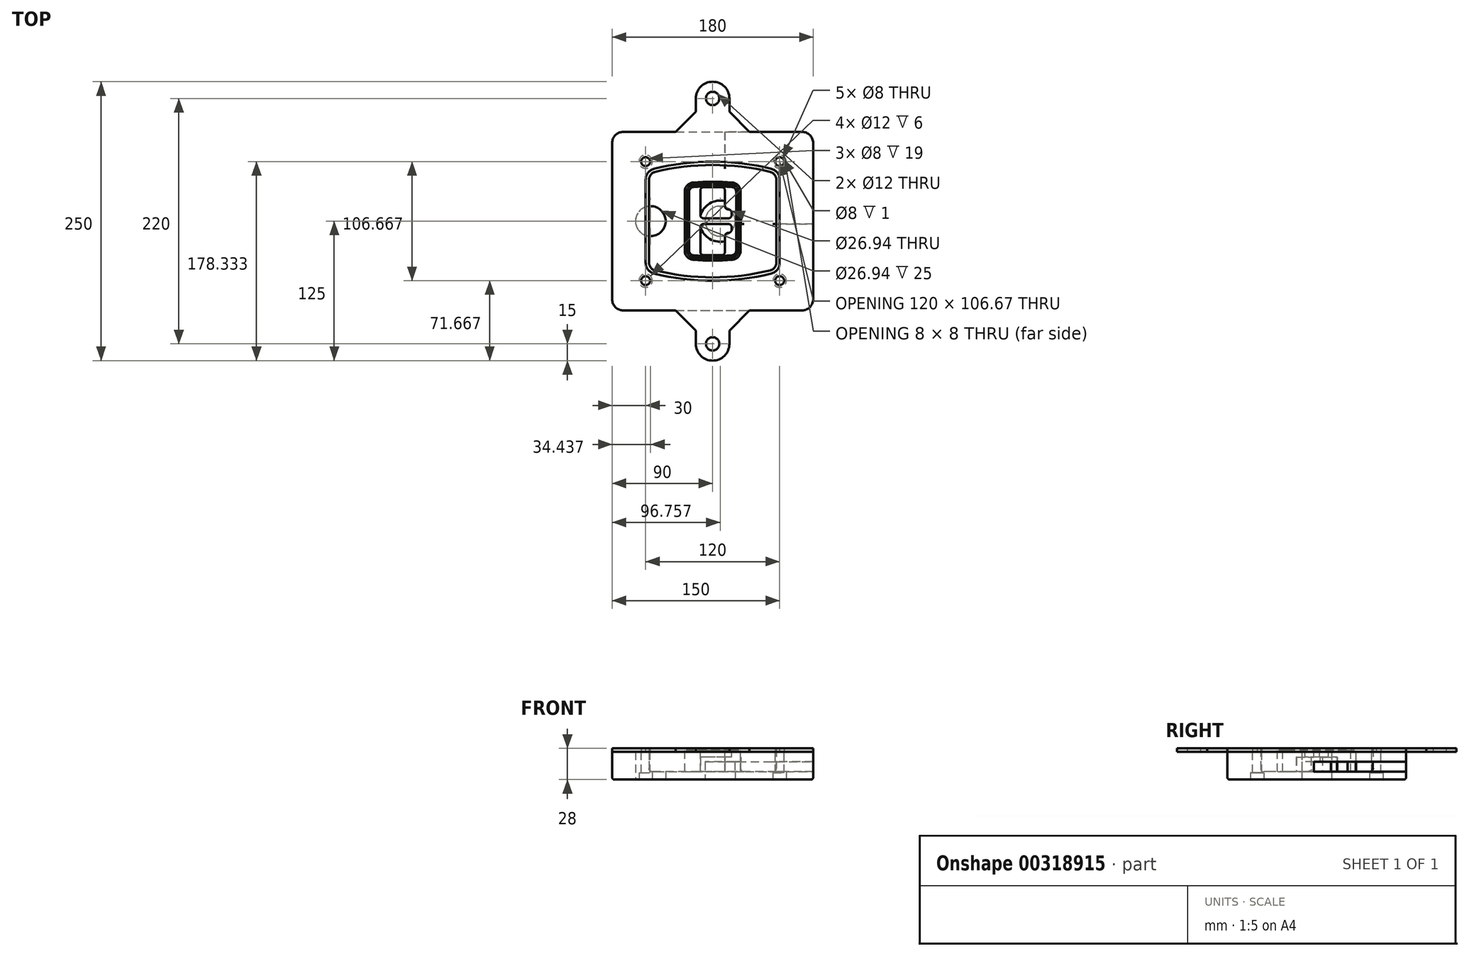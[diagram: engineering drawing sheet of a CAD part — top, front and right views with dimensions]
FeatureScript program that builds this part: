
annotation { "Feature Type Name" : "Feature", "Feature Type Description" : "" }
export const myFeature = defineFeature(function(context is Context, id is Id, definition is map)
    precondition{}
    {
        {
            var Q0;
            Q0=qCreatedBy(makeId("Top.planeOp"),FACE);
            var sketch = newSketch(context, id + "F0", { "sketchPlane" : qUnion([Q0])});
            skPoint(sketch, "E0.rect.middle", {"position": v(0, 0) * mm});
            skLineSegment(sketch, "E1.bottom", {"start": v(-80, -80) * mm, "end": v(80, -80) * mm});
            skLineSegment(sketch, "E1.top", {"start": v(-80, 80) * mm, "end": v(80, 80) * mm});
            skLineSegment(sketch, "E1.left", {"start": v(-90, -70) * mm, "end": v(-90, 70) * mm});
            skLineSegment(sketch, "E1.right", {"start": v(90, -70) * mm, "end": v(90, 70) * mm});
            skLineSegment(sketch, "E2", {"start": v(-90, 80) * mm, "end": v(90, -80) * mm, "construction": true});
            skLineSegment(sketch, "E3", {"start": v(90, 80) * mm, "end": v(-90, -80) * mm, "construction": true});
            skCircle(sketch, "E4", {"center": v(-60, 53.33) * mm, "radius": 4 * mm});
            skCircle(sketch, "E5", {"center": v(60, 53.33) * mm, "radius": 4 * mm});
            skCircle(sketch, "E6", {"center": v(60, -53.33) * mm, "radius": 4 * mm});
            skCircle(sketch, "E7", {"center": v(-60, -53.33) * mm, "radius": 4 * mm});
            skLineSegment(sketch, "E8", {"start": v(-60, 53.33) * mm, "end": v(60, 53.33) * mm, "construction": true});
            skLineSegment(sketch, "E9", {"start": v(60, 53.33) * mm, "end": v(60, -53.33) * mm, "construction": true});
            skLineSegment(sketch, "E10", {"start": v(60, -53.33) * mm, "end": v(-60, -53.33) * mm, "construction": true});
            skLineSegment(sketch, "E11", {"start": v(-60, -53.33) * mm, "end": v(-60, 53.33) * mm, "construction": true});
            skLineSegment(sketch, "E12", {"start": v(-60, 37.3) * mm, "end": v(-60, -37.3) * mm});
            skLineSegment(sketch, "E13", {"start": v(60, 37.3) * mm, "end": v(60, -37.3) * mm});
            skArc(sketch, "E14", {"start": v(52.38, 47.01) * mm, "mid": v(0, 53.33) * mm, "end": v(-52.38, 47.01) * mm});
            skArc(sketch, "E15", {"start": v(-52.38, -47.01) * mm, "mid": v(0, -53.33) * mm, "end": v(52.38, -47.01) * mm});
            skLineSegment(sketch, "E16", {"start": v(-60, 0) * mm, "end": v(60, 0) * mm, "construction": true});
            skPoint(sketch, "E17.visualSharp", {"position": v(-60, -45) * mm});
            skArc(sketch, "E17.filletArc", {"start": v(-60, -37.3) * mm, "mid": v(-57.87, -43.47) * mm, "end": v(-52.38, -47.01) * mm});
            skPoint(sketch, "E18.visualSharp", {"position": v(-60, 45) * mm});
            skArc(sketch, "E18.filletArc", {"start": v(-52.38, 47.01) * mm, "mid": v(-57.87, 43.47) * mm, "end": v(-60, 37.3) * mm});
            skPoint(sketch, "E19.visualSharp", {"position": v(60, 45) * mm});
            skArc(sketch, "E19.filletArc", {"start": v(60, 37.3) * mm, "mid": v(57.87, 43.47) * mm, "end": v(52.38, 47.01) * mm});
            skPoint(sketch, "E20.visualSharp", {"position": v(60, -45) * mm});
            skArc(sketch, "E20.filletArc", {"start": v(52.38, -47.01) * mm, "mid": v(57.87, -43.47) * mm, "end": v(60, -37.3) * mm});
            skPoint(sketch, "E21.visualSharp", {"position": v(-90, 80) * mm});
            skArc(sketch, "E21.filletArc", {"start": v(-80, 80) * mm, "mid": v(-87.07, 77.07) * mm, "end": v(-90, 70) * mm});
            skPoint(sketch, "E22.visualSharp", {"position": v(90, 80) * mm});
            skArc(sketch, "E22.filletArc", {"start": v(90, 70) * mm, "mid": v(87.07, 77.07) * mm, "end": v(80, 80) * mm});
            skPoint(sketch, "E23.visualSharp", {"position": v(90, -80) * mm});
            skArc(sketch, "E23.filletArc", {"start": v(80, -80) * mm, "mid": v(87.07, -77.07) * mm, "end": v(90, -70) * mm});
            skPoint(sketch, "E24.visualSharp", {"position": v(-90, -80) * mm});
            skArc(sketch, "E24.filletArc", {"start": v(-90, -70) * mm, "mid": v(-87.07, -77.07) * mm, "end": v(-80, -80) * mm});
            skArc(sketch, "E25.0", {"start": v(57, 37.3) * mm, "mid": v(55.5, 41.62) * mm, "end": v(51.67, 44.1) * mm});
            skLineSegment(sketch, "E25.1", {"start": v(57, 37.3) * mm, "end": v(57, -37.3) * mm});
            skArc(sketch, "E25.2", {"start": v(51.67, -44.1) * mm, "mid": v(55.5, -41.62) * mm, "end": v(57, -37.3) * mm});
            skArc(sketch, "E25.3", {"start": v(-51.67, -44.1) * mm, "mid": v(0, -50.33) * mm, "end": v(51.67, -44.1) * mm});
            skArc(sketch, "E25.4", {"start": v(-57, -37.3) * mm, "mid": v(-55.5, -41.62) * mm, "end": v(-51.67, -44.1) * mm});
            skArc(sketch, "E25.5", {"start": v(51.67, 44.1) * mm, "mid": v(0, 50.33) * mm, "end": v(-51.67, 44.1) * mm});
            skLineSegment(sketch, "E25.6", {"start": v(-57, 37.3) * mm, "end": v(-57, -37.3) * mm});
            skArc(sketch, "E25.7", {"start": v(-51.67, 44.1) * mm, "mid": v(-55.5, 41.62) * mm, "end": v(-57, 37.3) * mm});
            skArc(sketch, "E26.0", {"start": v(-53.33, 50.9) * mm, "mid": v(-61.01, 45.94) * mm, "end": v(-64, 37.3) * mm});
            skArc(sketch, "E26.1", {"start": v(53.33, 50.9) * mm, "mid": v(0, 57.33) * mm, "end": v(-53.33, 50.9) * mm});
            skArc(sketch, "E26.2", {"start": v(64, 37.3) * mm, "mid": v(61.01, 45.94) * mm, "end": v(53.33, 50.9) * mm});
            skLineSegment(sketch, "E26.3", {"start": v(64, 37.3) * mm, "end": v(64, -37.3) * mm});
            skArc(sketch, "E26.4", {"start": v(53.33, -50.9) * mm, "mid": v(61.01, -45.94) * mm, "end": v(64, -37.3) * mm});
            skLineSegment(sketch, "E26.5", {"start": v(-64, 37.3) * mm, "end": v(-64, -37.3) * mm});
            skArc(sketch, "E26.6", {"start": v(-53.33, -50.9) * mm, "mid": v(0, -57.33) * mm, "end": v(53.33, -50.9) * mm});
            skArc(sketch, "E26.7", {"start": v(-64, -37.3) * mm, "mid": v(-61.01, -45.94) * mm, "end": v(-53.33, -50.9) * mm});
            skSolve(sketch);
        }
        {
            var Q0;
            Q0=makeQuery(id+"F0.imprint","IMPRINT",FACE,{"disambiguationData":[TD([[makeQuery(id+"F0.imprint","IMPRINT",EDGE,{"derivedFrom":sQuery(id+"F0.wireOp",EDGE,"E1.bottom")}),1.0]])]});
            var Q1;
            Q1=makeQuery(id+"F0.imprint","IMPRINT",FACE,{"disambiguationData":[TD([[makeQuery(id+"F0.imprint","IMPRINT",EDGE,{"derivedFrom":sQuery(id+"F0.wireOp",EDGE,"E12")}),1.0]])]});
            var Q2;
            Q2=makeQuery(id+"F0.imprint","IMPRINT",FACE,{"disambiguationData":[TD([[makeQuery(id+"F0.imprint","IMPRINT",EDGE,{"derivedFrom":sQuery(id+"F0.wireOp",EDGE,"E25.0")}),1.0]])]});
            var Q3;
            Q3=makeQuery(id+"F0.imprint","IMPRINT",FACE,{"disambiguationData":[TD([[makeQuery(id+"F0.imprint","IMPRINT",EDGE,{"derivedFrom":sQuery(id+"F0.wireOp",EDGE,"E12")}),-1.0]])]});
            extrude(context, id + "F1", {"entities" : qUnion([Q0, Q1, Q2, Q3]), "oppositeDirection" : true, "depth" : 25 * mm});
        }
        {
            var Q0;
            Q0=makeQuery(id+"F0.imprint","IMPRINT",FACE,{"disambiguationData":[TD([[makeQuery(id+"F0.imprint","IMPRINT",EDGE,{"derivedFrom":sQuery(id+"F0.wireOp",EDGE,"E12")}),1.0]])]});
            extrude(context, id + "F2", {"entities" : qUnion([Q0]), "operationType" : NewBodyOperationType.ADD, "depth" : 3 * mm});
        }
        {
            var Q0;
            Q0=makeQuery(id+"F0.imprint","IMPRINT",FACE,{"disambiguationData":[TD([[makeQuery(id+"F0.imprint","IMPRINT",EDGE,{"derivedFrom":sQuery(id+"F0.wireOp",EDGE,"E25.0")}),1.0]])]});
            extrude(context, id + "F3", {"entities" : qUnion([Q0]), "operationType" : NewBodyOperationType.REMOVE, "oppositeDirection" : true, "depth" : 18 * mm});
        }
        {
            var Q0;
            Q0=makeQuery(id+"F2.opExtrude","CAP_FACE",FACE,{"disambiguationData":[OSD([sQuery(id+"F0.wireOp",EDGE,"E12"),sQuery(id+"F0.wireOp",EDGE,"E13"),sQuery(id+"F0.wireOp",EDGE,"E14"),sQuery(id+"F0.wireOp",EDGE,"E15"),sQuery(id+"F0.wireOp",EDGE,"E17.filletArc"),sQuery(id+"F0.wireOp",EDGE,"E18.filletArc"),sQuery(id+"F0.wireOp",EDGE,"E19.filletArc"),sQuery(id+"F0.wireOp",EDGE,"E20.filletArc"),sQuery(id+"F0.wireOp",EDGE,"E25.0"),sQuery(id+"F0.wireOp",EDGE,"E25.1"),sQuery(id+"F0.wireOp",EDGE,"E25.2"),sQuery(id+"F0.wireOp",EDGE,"E25.3"),sQuery(id+"F0.wireOp",EDGE,"E25.4"),sQuery(id+"F0.wireOp",EDGE,"E25.5"),sQuery(id+"F0.wireOp",EDGE,"E25.6"),sQuery(id+"F0.wireOp",EDGE,"E25.7")])],"isStart":false});
            var sketch = newSketch(context, id + "F4", { "sketchPlane" : qUnion([Q0])});
            skArc(sketch, "E27.0", {"start": v(-17.7, -34.56) * mm, "mid": v(0, -35.33) * mm, "end": v(17.7, -34.56) * mm});
            skArc(sketch, "E28.0", {"start": v(17.7, 34.56) * mm, "mid": v(0, 35.33) * mm, "end": v(-17.7, 34.56) * mm});
            skLineSegment(sketch, "E29", {"start": v(-25, 26.59) * mm, "end": v(-25, -26.59) * mm});
            skLineSegment(sketch, "E30", {"start": v(25, 26.59) * mm, "end": v(25, -26.59) * mm});
            skLineSegment(sketch, "E31", {"start": v(-25, 33.78) * mm, "end": v(25, 33.78) * mm, "construction": true});
            skLineSegment(sketch, "E32", {"start": v(-25, -33.78) * mm, "end": v(25, -33.78) * mm, "construction": true});
            skPoint(sketch, "E33.visualSharp", {"position": v(-25, 33.78) * mm});
            skArc(sketch, "E33.filletArc", {"start": v(-17.7, 34.56) * mm, "mid": v(-22.9, 32) * mm, "end": v(-25, 26.59) * mm});
            skPoint(sketch, "E34.visualSharp", {"position": v(25, 33.78) * mm});
            skArc(sketch, "E34.filletArc", {"start": v(25, 26.59) * mm, "mid": v(22.9, 32) * mm, "end": v(17.7, 34.56) * mm});
            skPoint(sketch, "E35.visualSharp", {"position": v(25, -33.78) * mm});
            skArc(sketch, "E35.filletArc", {"start": v(17.7, -34.56) * mm, "mid": v(22.9, -32) * mm, "end": v(25, -26.59) * mm});
            skPoint(sketch, "E36.visualSharp", {"position": v(-25, -33.78) * mm});
            skArc(sketch, "E36.filletArc", {"start": v(-25, -26.59) * mm, "mid": v(-22.9, -32) * mm, "end": v(-17.7, -34.56) * mm});
            skArc(sketch, "E37.0", {"start": v(51.67, 44.1) * mm, "mid": v(0, 50.33) * mm, "end": v(-51.67, 44.1) * mm});
            skArc(sketch, "E37.1", {"start": v(-51.67, 44.1) * mm, "mid": v(-55.5, 41.62) * mm, "end": v(-57, 37.3) * mm});
            skLineSegment(sketch, "E37.2", {"start": v(-57, 37.3) * mm, "end": v(-57, -37.3) * mm});
            skArc(sketch, "E37.3", {"start": v(-57, -37.3) * mm, "mid": v(-55.5, -41.62) * mm, "end": v(-51.67, -44.1) * mm});
            skArc(sketch, "E37.4", {"start": v(-51.67, -44.1) * mm, "mid": v(0, -50.33) * mm, "end": v(51.67, -44.1) * mm});
            skArc(sketch, "E37.5", {"start": v(51.67, -44.1) * mm, "mid": v(55.5, -41.62) * mm, "end": v(57, -37.3) * mm});
            skLineSegment(sketch, "E37.6", {"start": v(57, 37.3) * mm, "end": v(57, -37.3) * mm});
            skArc(sketch, "E37.7", {"start": v(57, 37.3) * mm, "mid": v(55.5, 41.62) * mm, "end": v(51.67, 44.1) * mm});
            skLineSegment(sketch, "E38.0", {"start": v(23, 26.59) * mm, "end": v(23, -26.59) * mm});
            skArc(sketch, "E38.1", {"start": v(17.53, -32.56) * mm, "mid": v(21.42, -30.64) * mm, "end": v(23, -26.59) * mm});
            skArc(sketch, "E38.2", {"start": v(-17.53, -32.56) * mm, "mid": v(0, -33.33) * mm, "end": v(17.53, -32.56) * mm});
            skArc(sketch, "E38.3", {"start": v(-23, -26.59) * mm, "mid": v(-21.42, -30.64) * mm, "end": v(-17.53, -32.56) * mm});
            skLineSegment(sketch, "E38.4", {"start": v(-23, 26.59) * mm, "end": v(-23, -26.59) * mm});
            skArc(sketch, "E38.5", {"start": v(23, 26.59) * mm, "mid": v(21.42, 30.64) * mm, "end": v(17.53, 32.56) * mm});
            skArc(sketch, "E38.6", {"start": v(-17.53, 32.56) * mm, "mid": v(-21.42, 30.64) * mm, "end": v(-23, 26.59) * mm});
            skArc(sketch, "E38.7", {"start": v(17.53, 32.56) * mm, "mid": v(0, 33.33) * mm, "end": v(-17.53, 32.56) * mm});
            skArc(sketch, "E39.0", {"start": v(21, 26.59) * mm, "mid": v(19.95, 29.29) * mm, "end": v(17.35, 30.57) * mm});
            skLineSegment(sketch, "E39.1", {"start": v(21, 26.59) * mm, "end": v(21, -26.59) * mm});
            skArc(sketch, "E39.2", {"start": v(17.35, -30.57) * mm, "mid": v(19.95, -29.29) * mm, "end": v(21, -26.59) * mm});
            skArc(sketch, "E39.3", {"start": v(-17.35, -30.57) * mm, "mid": v(0, -31.33) * mm, "end": v(17.35, -30.57) * mm});
            skArc(sketch, "E39.4", {"start": v(-21, -26.59) * mm, "mid": v(-19.95, -29.29) * mm, "end": v(-17.35, -30.57) * mm});
            skArc(sketch, "E39.5", {"start": v(17.35, 30.57) * mm, "mid": v(0, 31.33) * mm, "end": v(-17.35, 30.57) * mm});
            skLineSegment(sketch, "E39.6", {"start": v(-21, 26.59) * mm, "end": v(-21, -26.59) * mm});
            skArc(sketch, "E39.7", {"start": v(-17.35, 30.57) * mm, "mid": v(-19.95, 29.29) * mm, "end": v(-21, 26.59) * mm});
            skLineSegment(sketch, "E40", {"start": v(-25, 0) * mm, "end": v(25, 0) * mm, "construction": true});
            skLineSegment(sketch, "E41", {"start": v(-11, 5.5) * mm, "end": v(-11, 27.5) * mm});
            skLineSegment(sketch, "E42", {"start": v(-8, 30.5) * mm, "end": v(8, 30.5) * mm});
            skLineSegment(sketch, "E43", {"start": v(11, 27.5) * mm, "end": v(11, 13.5) * mm});
            skLineSegment(sketch, "E44", {"start": v(14, 10.5) * mm, "end": v(14, 10.5) * mm});
            skLineSegment(sketch, "E45", {"start": v(17, 7.5) * mm, "end": v(17, 5.5) * mm});
            skLineSegment(sketch, "E46", {"start": v(14, 2.5) * mm, "end": v(-8, 2.5) * mm});
            skPoint(sketch, "E47.visualSharp", {"position": v(-11, 30.5) * mm});
            skArc(sketch, "E47.filletArc", {"start": v(-8, 30.5) * mm, "mid": v(-10.12, 29.62) * mm, "end": v(-11, 27.5) * mm});
            skPoint(sketch, "E48.visualSharp", {"position": v(11, 30.5) * mm});
            skArc(sketch, "E48.filletArc", {"start": v(11, 27.5) * mm, "mid": v(10.12, 29.62) * mm, "end": v(8, 30.5) * mm});
            skPoint(sketch, "E49.visualSharp", {"position": v(11, 10.5) * mm});
            skArc(sketch, "E49.filletArc", {"start": v(11, 13.5) * mm, "mid": v(11.88, 11.38) * mm, "end": v(14, 10.5) * mm});
            skPoint(sketch, "E50.visualSharp", {"position": v(17, 10.5) * mm});
            skArc(sketch, "E50.filletArc", {"start": v(17, 7.5) * mm, "mid": v(16.12, 9.62) * mm, "end": v(14, 10.5) * mm});
            skPoint(sketch, "E51.visualSharp", {"position": v(17, 2.5) * mm});
            skArc(sketch, "E51.filletArc", {"start": v(14, 2.5) * mm, "mid": v(16.12, 3.38) * mm, "end": v(17, 5.5) * mm});
            skPoint(sketch, "E52.visualSharp", {"position": v(-11, 2.5) * mm});
            skArc(sketch, "E52.filletArc", {"start": v(-11, 5.5) * mm, "mid": v(-10.12, 3.38) * mm, "end": v(-8, 2.5) * mm});
            skLineSegment(sketch, "E53.0.MirrorCS", {"start": v(14, -2.5) * mm, "end": v(-8, -2.5) * mm});
            skArc(sketch, "E54.0.MirrorCS", {"start": v(-11, -5.5) * mm, "mid": v(-10.12, -3.38) * mm, "end": v(-8, -2.5) * mm});
            skLineSegment(sketch, "E55.0.MirrorCS", {"start": v(-11, -5.5) * mm, "end": v(-11, -27.5) * mm});
            skArc(sketch, "E56.0.MirrorCS", {"start": v(-8, -30.5) * mm, "mid": v(-10.12, -29.62) * mm, "end": v(-11, -27.5) * mm});
            skLineSegment(sketch, "E57.0.MirrorCS", {"start": v(-8, -30.5) * mm, "end": v(8, -30.5) * mm});
            skArc(sketch, "E58.0.MirrorCS", {"start": v(11, -27.5) * mm, "mid": v(10.12, -29.62) * mm, "end": v(8, -30.5) * mm});
            skLineSegment(sketch, "E59.0.MirrorCS", {"start": v(11, -27.5) * mm, "end": v(11, -13.5) * mm});
            skArc(sketch, "E60.0.MirrorCS", {"start": v(11, -13.5) * mm, "mid": v(11.88, -11.38) * mm, "end": v(14, -10.5) * mm});
            skArc(sketch, "E61.0.MirrorCS", {"start": v(17, -7.5) * mm, "mid": v(16.12, -9.62) * mm, "end": v(14, -10.5) * mm});
            skLineSegment(sketch, "E62.0.MirrorCS", {"start": v(17, -7.5) * mm, "end": v(17, -5.5) * mm});
            skArc(sketch, "E63.0.MirrorCS", {"start": v(14, -2.5) * mm, "mid": v(16.12, -3.38) * mm, "end": v(17, -5.5) * mm});
            skSolve(sketch);
        }
        {
            var Q0;
            Q0=makeQuery(id+"F4.imprint","IMPRINT",FACE,{"disambiguationData":[TD([[makeQuery(id+"F4.imprint","IMPRINT",EDGE,{"derivedFrom":sQuery(id+"F4.wireOp",EDGE,"E27.0")}),1.0]])]});
            var Q1;
            Q1=makeQuery(id+"F4.imprint","IMPRINT",FACE,{"disambiguationData":[TD([[makeQuery(id+"F4.imprint","IMPRINT",EDGE,{"derivedFrom":sQuery(id+"F4.wireOp",EDGE,"E38.0")}),-1.0]])]});
            var Q2;
            Q2=makeQuery(id+"F4.imprint","IMPRINT",FACE,{"disambiguationData":[TD([[makeQuery(id+"F4.imprint","IMPRINT",EDGE,{"derivedFrom":sQuery(id+"F4.wireOp",EDGE,"E39.0")}),1.0]])]});
            extrude(context, id + "F5", {"entities" : qUnion([Q0, Q1, Q2]), "operationType" : NewBodyOperationType.ADD, "endBound" : BoundingType.UP_TO_NEXT, "oppositeDirection" : true, "depth" : 25 * mm});
        }
        {
            var Q0;
            Q0=makeQuery(id+"F4.imprint","IMPRINT",FACE,{"disambiguationData":[TD([[makeQuery(id+"F4.imprint","IMPRINT",EDGE,{"derivedFrom":sQuery(id+"F4.wireOp",EDGE,"E38.0")}),-1.0]])]});
            extrude(context, id + "F6", {"entities" : qUnion([Q0]), "operationType" : NewBodyOperationType.REMOVE, "oppositeDirection" : true, "depth" : 2 * mm});
        }
        {
            var Q0;
            Q0=makeQuery(id+"F1.opExtrude","CAP_FACE",FACE,{"disambiguationData":[OSD([sQuery(id+"F0.wireOp",EDGE,"E1.bottom"),sQuery(id+"F0.wireOp",EDGE,"E1.top"),sQuery(id+"F0.wireOp",EDGE,"E1.left"),sQuery(id+"F0.wireOp",EDGE,"E1.right"),sQuery(id+"F0.wireOp",EDGE,"E4"),sQuery(id+"F0.wireOp",EDGE,"E5"),sQuery(id+"F0.wireOp",EDGE,"E6"),sQuery(id+"F0.wireOp",EDGE,"E7"),sQuery(id+"F0.wireOp",EDGE,"E21.filletArc"),sQuery(id+"F0.wireOp",EDGE,"E22.filletArc"),sQuery(id+"F0.wireOp",EDGE,"E23.filletArc"),sQuery(id+"F0.wireOp",EDGE,"E24.filletArc")])],"isStart":false});
            var sketch = newSketch(context, id + "F7", { "sketchPlane" : qUnion([Q0])});
            skCircle(sketch, "E64", {"center": v(6.76, 0) * mm, "radius": 13.47 * mm});
            skCircle(sketch, "E65", {"center": v(-55.56, 0) * mm, "radius": 13.47 * mm});
            skLineSegment(sketch, "E66", {"start": v(90, 0) * mm, "end": v(-90, 0) * mm});
            skCircle(sketch, "E67", {"center": v(6.76, 0) * mm, "radius": 18.47 * mm});
            skCircle(sketch, "E68", {"center": v(60, -53.33) * mm, "radius": 6 * mm});
            skCircle(sketch, "E69", {"center": v(-60, -53.33) * mm, "radius": 6 * mm});
            skCircle(sketch, "E70", {"center": v(-60, 53.33) * mm, "radius": 6 * mm});
            skCircle(sketch, "E71", {"center": v(60, 53.33) * mm, "radius": 6 * mm});
            skSolve(sketch);
        }
        {
            var Q0;
            {var subQ1=sQuery(id+"F7.wireOp",EDGE,"E66");var subQ4=sQuery(id+"F7.wireOp",EDGE,"E64");var subQ6=makeQuery(id+"F7.imprint","INTERSECT",VERTEX,{"disambiguationData":[OD(0.0)],"derivedFrom":[subQ4,subQ1]});Q0=makeQuery(id+"F7.imprint","IMPRINT",FACE,{"disambiguationData":[TD([[makeQuery(id+"F7.imprint","IMPRINT",EDGE,{"disambiguationData":[TD([[subQ6,-1.0]])],"derivedFrom":subQ4}),-1.0]])]});}
            var Q1;
            {var subQ0=sQuery(id+"F7.wireOp",EDGE,"E66");var subQ1=sQuery(id+"F7.wireOp",EDGE,"E64");var subQ3=makeQuery(id+"F7.imprint","INTERSECT",VERTEX,{"disambiguationData":[OD(0.0)],"derivedFrom":[subQ1,subQ0]});Q1=makeQuery(id+"F7.imprint","IMPRINT",FACE,{"disambiguationData":[TD([[makeQuery(id+"F7.imprint","IMPRINT",EDGE,{"disambiguationData":[TD([[subQ3,-1.0]])],"derivedFrom":subQ1}),1.0]])]});}
            var Q2;
            {var subQ0=sQuery(id+"F7.wireOp",EDGE,"E66");var subQ1=sQuery(id+"F7.wireOp",EDGE,"E64");var subQ3=makeQuery(id+"F7.imprint","INTERSECT",VERTEX,{"disambiguationData":[OD(0.0)],"derivedFrom":[subQ1,subQ0]});Q2=makeQuery(id+"F7.imprint","IMPRINT",FACE,{"disambiguationData":[TD([[makeQuery(id+"F7.imprint","IMPRINT",EDGE,{"disambiguationData":[TD([[subQ3,1.0]])],"derivedFrom":subQ1}),1.0]])]});}
            var Q3;
            {var subQ1=sQuery(id+"F7.wireOp",EDGE,"E66");var subQ4=sQuery(id+"F7.wireOp",EDGE,"E64");var subQ6=makeQuery(id+"F7.imprint","INTERSECT",VERTEX,{"disambiguationData":[OD(0.0)],"derivedFrom":[subQ4,subQ1]});Q3=makeQuery(id+"F7.imprint","IMPRINT",FACE,{"disambiguationData":[TD([[makeQuery(id+"F7.imprint","IMPRINT",EDGE,{"disambiguationData":[TD([[subQ6,1.0]])],"derivedFrom":subQ4}),-1.0]])]});}
            extrude(context, id + "F8", {"entities" : qUnion([Q0, Q1, Q2, Q3]), "operationType" : NewBodyOperationType.ADD, "oppositeDirection" : true, "depth" : 20 * mm});
        }
        {
            var Q0;
            {var subQ0=sQuery(id+"F7.wireOp",EDGE,"E66");var subQ1=sQuery(id+"F7.wireOp",EDGE,"E64");var subQ3=makeQuery(id+"F7.imprint","INTERSECT",VERTEX,{"disambiguationData":[OD(0.0)],"derivedFrom":[subQ1,subQ0]});Q0=makeQuery(id+"F7.imprint","IMPRINT",FACE,{"disambiguationData":[TD([[makeQuery(id+"F7.imprint","IMPRINT",EDGE,{"disambiguationData":[TD([[subQ3,-1.0]])],"derivedFrom":subQ1}),1.0]])]});}
            var Q1;
            {var subQ0=sQuery(id+"F7.wireOp",EDGE,"E66");var subQ1=sQuery(id+"F7.wireOp",EDGE,"E64");var subQ3=makeQuery(id+"F7.imprint","INTERSECT",VERTEX,{"disambiguationData":[OD(0.0)],"derivedFrom":[subQ1,subQ0]});Q1=makeQuery(id+"F7.imprint","IMPRINT",FACE,{"disambiguationData":[TD([[makeQuery(id+"F7.imprint","IMPRINT",EDGE,{"disambiguationData":[TD([[subQ3,1.0]])],"derivedFrom":subQ1}),1.0]])]});}
            extrude(context, id + "F9", {"entities" : qUnion([Q0, Q1]), "operationType" : NewBodyOperationType.REMOVE, "oppositeDirection" : true, "depth" : 16 * mm});
        }
        {
            var Q0;
            {var subQ0=sQuery(id+"F7.wireOp",EDGE,"E66");var subQ1=sQuery(id+"F7.wireOp",EDGE,"E65");var subQ3=makeQuery(id+"F7.imprint","INTERSECT",VERTEX,{"disambiguationData":[OD(0.0)],"derivedFrom":[subQ1,subQ0]});Q0=makeQuery(id+"F7.imprint","IMPRINT",FACE,{"disambiguationData":[TD([[makeQuery(id+"F7.imprint","IMPRINT",EDGE,{"disambiguationData":[TD([[subQ3,-1.0]])],"derivedFrom":subQ1}),1.0]])]});}
            var Q1;
            {var subQ0=sQuery(id+"F7.wireOp",EDGE,"E66");var subQ1=sQuery(id+"F7.wireOp",EDGE,"E65");var subQ3=makeQuery(id+"F7.imprint","INTERSECT",VERTEX,{"disambiguationData":[OD(0.0)],"derivedFrom":[subQ1,subQ0]});Q1=makeQuery(id+"F7.imprint","IMPRINT",FACE,{"disambiguationData":[TD([[makeQuery(id+"F7.imprint","IMPRINT",EDGE,{"disambiguationData":[TD([[subQ3,1.0]])],"derivedFrom":subQ1}),1.0]])]});}
            extrude(context, id + "F10", {"entities" : qUnion([Q0, Q1]), "operationType" : NewBodyOperationType.REMOVE, "oppositeDirection" : true, "depth" : 25 * mm});
        }
        {
            var Q0;
            Q0=makeQuery(id+"F7.imprint","IMPRINT",FACE,{"disambiguationData":[TD([[makeQuery(id+"F7.imprint","IMPRINT",EDGE,{"derivedFrom":sQuery(id+"F7.wireOp",EDGE,"E68")}),1.0]])]});
            var Q1;
            Q1=makeQuery(id+"F7.imprint","IMPRINT",FACE,{"disambiguationData":[TD([[makeQuery(id+"F7.imprint","IMPRINT",EDGE,{"derivedFrom":makeQuery(id+"F1.opExtrude","CAP_EDGE",EDGE,{"disambiguationData":[OSD([sQuery(id+"F0.wireOp",EDGE,"E5")])],"isStart":false})}),-1.0]])]});
            var Q2;
            Q2=makeQuery(id+"F7.imprint","IMPRINT",FACE,{"disambiguationData":[TD([[makeQuery(id+"F7.imprint","IMPRINT",EDGE,{"derivedFrom":sQuery(id+"F7.wireOp",EDGE,"E69")}),1.0]])]});
            var Q3;
            Q3=makeQuery(id+"F7.imprint","IMPRINT",FACE,{"disambiguationData":[TD([[makeQuery(id+"F7.imprint","IMPRINT",EDGE,{"derivedFrom":makeQuery(id+"F1.opExtrude","CAP_EDGE",EDGE,{"disambiguationData":[OSD([sQuery(id+"F0.wireOp",EDGE,"E4")])],"isStart":false})}),-1.0]])]});
            var Q4;
            Q4=makeQuery(id+"F7.imprint","IMPRINT",FACE,{"disambiguationData":[TD([[makeQuery(id+"F7.imprint","IMPRINT",EDGE,{"derivedFrom":sQuery(id+"F7.wireOp",EDGE,"E70")}),1.0]])]});
            var Q5;
            Q5=makeQuery(id+"F7.imprint","IMPRINT",FACE,{"disambiguationData":[TD([[makeQuery(id+"F7.imprint","IMPRINT",EDGE,{"derivedFrom":makeQuery(id+"F1.opExtrude","CAP_EDGE",EDGE,{"disambiguationData":[OSD([sQuery(id+"F0.wireOp",EDGE,"E7")])],"isStart":false})}),-1.0]])]});
            var Q6;
            Q6=makeQuery(id+"F7.imprint","IMPRINT",FACE,{"disambiguationData":[TD([[makeQuery(id+"F7.imprint","IMPRINT",EDGE,{"derivedFrom":sQuery(id+"F7.wireOp",EDGE,"E71")}),1.0]])]});
            var Q7;
            Q7=makeQuery(id+"F7.imprint","IMPRINT",FACE,{"disambiguationData":[TD([[makeQuery(id+"F7.imprint","IMPRINT",EDGE,{"derivedFrom":makeQuery(id+"F1.opExtrude","CAP_EDGE",EDGE,{"disambiguationData":[OSD([sQuery(id+"F0.wireOp",EDGE,"E6")])],"isStart":false})}),-1.0]])]});
            extrude(context, id + "F11", {"entities" : qUnion([Q0, Q1, Q2, Q3, Q4, Q5, Q6, Q7]), "operationType" : NewBodyOperationType.REMOVE, "oppositeDirection" : true, "depth" : 6 * mm});
        }
        {
            var Q0;
            Q0=makeQuery(id+"F9.boolean.opBoolean","COPY",FACE,{"derivedFrom":makeQuery(id+"F9.opExtrude","CAP_FACE",FACE,{"disambiguationData":[OSD([sQuery(id+"F7.wireOp",EDGE,"E64")])],"isStart":false})});
            var sketch = newSketch(context, id + "F12", { "sketchPlane" : qUnion([Q0])});
            skArc(sketch, "E72.0", {"start": v(11, -88.19) * mm, "mid": v(97.1, -83.6) * mm, "end": v(92.5, 2.5) * mm});
            skLineSegment(sketch, "E72.1", {"start": v(11, -17.97) * mm, "end": v(11, -17.97) * mm});
            skLineSegment(sketch, "E73", {"start": v(92.5, -105.13) * mm, "end": v(102.3, -105.13) * mm});
            skLineSegment(sketch, "E74.0", {"start": v(92.5, 2.5) * mm, "end": v(14, 2.5) * mm});
            skArc(sketch, "E74.1", {"start": v(14, 2.5) * mm, "mid": v(16.12, 3.38) * mm, "end": v(17, 5.5) * mm});
            skLineSegment(sketch, "E74.2", {"start": v(17, 7.5) * mm, "end": v(17, 5.5) * mm});
            skArc(sketch, "E74.3", {"start": v(17, 7.5) * mm, "mid": v(16.12, 9.62) * mm, "end": v(14, 10.5) * mm});
            skArc(sketch, "E74.4", {"start": v(11, 13.5) * mm, "mid": v(11.88, 11.38) * mm, "end": v(14, 10.5) * mm});
            skLineSegment(sketch, "E74.5", {"start": v(11, 13.5) * mm, "end": v(11, -88.19) * mm});
            skLineSegment(sketch, "E74.7", {"start": v(92.5, -2.5) * mm, "end": v(14, -2.5) * mm});
            skArc(sketch, "E74.8", {"start": v(14, -2.5) * mm, "mid": v(16.12, -3.38) * mm, "end": v(17, -5.5) * mm});
            skLineSegment(sketch, "E74.9", {"start": v(17, -7.5) * mm, "end": v(17, -5.5) * mm});
            skArc(sketch, "E74.10", {"start": v(17, -7.5) * mm, "mid": v(16.12, -9.62) * mm, "end": v(14, -10.5) * mm});
            skArc(sketch, "E74.11", {"start": v(11, -13.5) * mm, "mid": v(11.88, -11.38) * mm, "end": v(14, -10.5) * mm});
            skLineSegment(sketch, "E74.12", {"start": v(11, -17.97) * mm, "end": v(11, -13.5) * mm});
            skPoint(sketch, "E75.orphan", {"position": v(11, -27.5) * mm});
            skPoint(sketch, "E76.orphan", {"position": v(-8, -2.5) * mm});
            skPoint(sketch, "E77.orphan", {"position": v(-8, 2.5) * mm});
            skPoint(sketch, "E78.orphan", {"position": v(11, 27.5) * mm});
            skSolve(sketch);
        }
        {
            var Q0;
            {var subQ7=sQuery(id+"F12.wireOp",EDGE,"E72.0");var subQ14=sQuery(id+"F12.wireOp",EDGE,"E72.1");var subQ16=sQuery(id+"F12.wireOp",EDGE,"E74.1");var subQ18=sQuery(id+"F12.wireOp",EDGE,"E74.8");Q0=qUnion([makeQuery(id+"F12.imprint","IMPRINT",FACE,{"disambiguationData":[TD([[makeQuery(id+"F12.imprint","IMPRINT",EDGE,{"derivedFrom":subQ7}),1.0]])]}),makeQuery(id+"F12.imprint","IMPRINT",FACE,{"disambiguationData":[TD([[makeQuery(id+"F12.imprint","IMPRINT",EDGE,{"derivedFrom":subQ14}),1.0]])]}),makeQuery(id+"F12.imprint","IMPRINT",FACE,{"disambiguationData":[TD([[makeQuery(id+"F12.imprint","IMPRINT",EDGE,{"derivedFrom":subQ16}),1.0]])]}),makeQuery(id+"F12.imprint","IMPRINT",FACE,{"disambiguationData":[TD([[makeQuery(id+"F12.imprint","IMPRINT",EDGE,{"derivedFrom":subQ18}),-1.0]])]})]);}
            var Q1;
            Q1=makeQuery(id+"F5.boolean.opBoolean","SPLIT",FACE,{"disambiguationData":[TD([makeQuery(id+"F5.opExtrude","SWEPT_FACE",FACE,{"disambiguationData":[OSD([sQuery(id+"F4.wireOp",EDGE,"E41")])]})])],"derivedFrom":makeQuery(id+"F3.boolean.opBoolean","COPY",FACE,{"derivedFrom":makeQuery(id+"F3.opExtrude","CAP_FACE",FACE,{"disambiguationData":[OSD([sQuery(id+"F0.wireOp",EDGE,"E25.0"),sQuery(id+"F0.wireOp",EDGE,"E25.1"),sQuery(id+"F0.wireOp",EDGE,"E25.2"),sQuery(id+"F0.wireOp",EDGE,"E25.3"),sQuery(id+"F0.wireOp",EDGE,"E25.4"),sQuery(id+"F0.wireOp",EDGE,"E25.5"),sQuery(id+"F0.wireOp",EDGE,"E25.6"),sQuery(id+"F0.wireOp",EDGE,"E25.7")])],"isStart":false})})});
            extrude(context, id + "F13", {"entities" : qUnion([Q0]), "operationType" : NewBodyOperationType.REMOVE, "endBound" : BoundingType.UP_TO_SURFACE, "endBoundEntityFace" : qUnion([Q1]), "depth" : 25 * mm});
        }
        {
            var Q0;
            Q0=makeQuery(id+"F3.boolean.opBoolean","COPY",EDGE,{"derivedFrom":makeQuery(id+"F3.opExtrude","CAP_EDGE",EDGE,{"disambiguationData":[OSD([sQuery(id+"F0.wireOp",EDGE,"E25.6")])],"isStart":false})});
            var Q1;
            Q1=makeQuery(id+"F8.boolean.opBoolean","INTERSECT",EDGE,{"derivedFrom":[makeQuery(id+"F5.opExtrude","SWEPT_FACE",FACE,{"disambiguationData":[OSD([sQuery(id+"F4.wireOp",EDGE,"E30")])]}),makeQuery(id+"F8.opExtrude","CAP_FACE",FACE,{"disambiguationData":[OSD([sQuery(id+"F7.wireOp",EDGE,"E67")])],"isStart":false})]});
            var Q2;
            Q2=makeQuery(id+"F8.boolean.opBoolean","INTERSECT",EDGE,{"disambiguationData":[OD(1.0)],"derivedFrom":[makeQuery(id+"F5.opExtrude","SWEPT_FACE",FACE,{"disambiguationData":[OSD([sQuery(id+"F4.wireOp",EDGE,"E30")])]}),makeQuery(id+"F8.opExtrude","SWEPT_FACE",FACE,{"disambiguationData":[OSD([sQuery(id+"F7.wireOp",EDGE,"E67")])]})]});
            var Q3;
            {var subQ0=makeQuery(id+"F3.boolean.opBoolean","COPY",FACE,{"derivedFrom":makeQuery(id+"F3.opExtrude","CAP_FACE",FACE,{"disambiguationData":[OSD([sQuery(id+"F0.wireOp",EDGE,"E25.0"),sQuery(id+"F0.wireOp",EDGE,"E25.1"),sQuery(id+"F0.wireOp",EDGE,"E25.2"),sQuery(id+"F0.wireOp",EDGE,"E25.3"),sQuery(id+"F0.wireOp",EDGE,"E25.4"),sQuery(id+"F0.wireOp",EDGE,"E25.5"),sQuery(id+"F0.wireOp",EDGE,"E25.6"),sQuery(id+"F0.wireOp",EDGE,"E25.7")])],"isStart":false})});var subQ1=sQuery(id+"F4.wireOp",EDGE,"E30");Q3=makeQuery(id+"F8.boolean.opBoolean","SPLIT",EDGE,{"disambiguationData":[TD([makeQuery(id+"F5.opExtrude","SWEPT_FACE",FACE,{"disambiguationData":[OSD([sQuery(id+"F4.wireOp",EDGE,"E35.filletArc")])]})])],"derivedFrom":makeQuery(id+"F5.opExtrude","TWEAK_EDGE",EDGE,{"derivedFrom":[subQ0,makeQuery(id+"F4.imprint","IMPRINT",EDGE,{"derivedFrom":subQ1})]})});}
            var Q4;
            {var subQ0=sQuery(id+"F0.wireOp",EDGE,"E25.0");var subQ1=sQuery(id+"F0.wireOp",EDGE,"E25.1");var subQ2=sQuery(id+"F0.wireOp",EDGE,"E25.2");var subQ3=sQuery(id+"F0.wireOp",EDGE,"E25.3");var subQ4=sQuery(id+"F0.wireOp",EDGE,"E25.4");var subQ5=sQuery(id+"F0.wireOp",EDGE,"E25.5");var subQ6=sQuery(id+"F0.wireOp",EDGE,"E25.6");var subQ7=sQuery(id+"F0.wireOp",EDGE,"E25.7");Q4=makeQuery(id+"F8.boolean.opBoolean","INTERSECT",EDGE,{"derivedFrom":[makeQuery(id+"F5.boolean.opBoolean","SPLIT",FACE,{"disambiguationData":[TD([makeQuery(id+"F2.opExtrude","SWEPT_FACE",FACE,{"disambiguationData":[OSD([subQ0])]})])],"derivedFrom":makeQuery(id+"F3.boolean.opBoolean","COPY",FACE,{"derivedFrom":makeQuery(id+"F3.opExtrude","CAP_FACE",FACE,{"disambiguationData":[OSD([subQ0,subQ1,subQ2,subQ3,subQ4,subQ5,subQ6,subQ7])],"isStart":false})})}),makeQuery(id+"F8.opExtrude","SWEPT_FACE",FACE,{"disambiguationData":[OSD([sQuery(id+"F7.wireOp",EDGE,"E67")])]})]});}
            var Q5;
            Q5=makeQuery(id+"F8.boolean.opBoolean","INTERSECT",EDGE,{"disambiguationData":[OD(0.0)],"derivedFrom":[makeQuery(id+"F5.opExtrude","SWEPT_FACE",FACE,{"disambiguationData":[OSD([sQuery(id+"F4.wireOp",EDGE,"E30")])]}),makeQuery(id+"F8.opExtrude","SWEPT_FACE",FACE,{"disambiguationData":[OSD([sQuery(id+"F7.wireOp",EDGE,"E67")])]})]});
            fillet(context, id + "F14", {"entities" : qUnion([Q0, Q1, Q2, Q3, Q4, Q5]), "radius" : 3 * mm, "tangentPropagation" : true, "allowEdgeOverflow" : false});
        }
        {
            var Q0;
            Q0=makeQuery(id+"F1.opExtrude","CAP_EDGE",EDGE,{"disambiguationData":[OSD([sQuery(id+"F0.wireOp",EDGE,"E1.bottom")])],"isStart":false});
            fillet(context, id + "F15", {"entities" : qUnion([Q0]), "radius" : 2 * mm, "tangentPropagation" : true, "allowEdgeOverflow" : false});
        }
        {
            var Q0;
            {var subQ0=sQuery(id+"F0.wireOp",EDGE,"E21.filletArc");var subQ1=sQuery(id+"F0.wireOp",EDGE,"E7");var subQ2=sQuery(id+"F0.wireOp",EDGE,"E6");var subQ3=sQuery(id+"F0.wireOp",EDGE,"E5");var subQ4=sQuery(id+"F0.wireOp",EDGE,"E4");var subQ5=sQuery(id+"F0.wireOp",EDGE,"E22.filletArc");var subQ6=sQuery(id+"F0.wireOp",EDGE,"E1.bottom");var subQ7=sQuery(id+"F0.wireOp",EDGE,"E1.right");var subQ8=sQuery(id+"F0.wireOp",EDGE,"E1.top");var subQ9=sQuery(id+"F0.wireOp",EDGE,"E1.left");var subQ10=sQuery(id+"F0.wireOp",EDGE,"E23.filletArc");var subQ11=sQuery(id+"F0.wireOp",EDGE,"E24.filletArc");Q0=makeQuery(id+"F2.boolean.opBoolean","SPLIT",FACE,{"disambiguationData":[TD([makeQuery(id+"F1.opExtrude","SWEPT_FACE",FACE,{"disambiguationData":[OSD([subQ6])]})])],"derivedFrom":makeQuery(id+"F1.opExtrude","CAP_FACE",FACE,{"disambiguationData":[OSD([subQ6,subQ8,subQ9,subQ7,subQ4,subQ3,subQ2,subQ1,subQ0,subQ5,subQ10,subQ11])],"isStart":true})});}
            var sketch = newSketch(context, id + "F16", { "sketchPlane" : qUnion([Q0])});
            skLineSegment(sketch, "E79.0", {"start": v(-90, -70) * mm, "end": v(-90, 70) * mm});
            skArc(sketch, "E79.1", {"start": v(-80, 80) * mm, "mid": v(-87.07, 77.07) * mm, "end": v(-90, 70) * mm});
            skLineSegment(sketch, "E79.2", {"start": v(-80, 80) * mm, "end": v(80, 80) * mm});
            skArc(sketch, "E79.3", {"start": v(90, 70) * mm, "mid": v(87.07, 77.07) * mm, "end": v(80, 80) * mm});
            skLineSegment(sketch, "E79.4", {"start": v(90, -70) * mm, "end": v(90, 70) * mm});
            skArc(sketch, "E79.5", {"start": v(80, -80) * mm, "mid": v(87.07, -77.07) * mm, "end": v(90, -70) * mm});
            skLineSegment(sketch, "E79.6", {"start": v(-80, -80) * mm, "end": v(80, -80) * mm});
            skArc(sketch, "E79.7", {"start": v(-90, -70) * mm, "mid": v(-87.07, -77.07) * mm, "end": v(-80, -80) * mm});
            skArc(sketch, "E79.8", {"start": v(-52.38, -47.01) * mm, "mid": v(0, -53.33) * mm, "end": v(52.38, -47.01) * mm});
            skLineSegment(sketch, "E80.0", {"start": v(-60, 37.3) * mm, "end": v(-60, -37.3) * mm});
            skLineSegment(sketch, "E80.1", {"start": v(60, 37.3) * mm, "end": v(60, -37.3) * mm});
            skArc(sketch, "E80.2", {"start": v(-60, -37.3) * mm, "mid": v(-57.87, -43.47) * mm, "end": v(-52.38, -47.01) * mm});
            skArc(sketch, "E80.4", {"start": v(-52.38, 47.01) * mm, "mid": v(-57.87, 43.47) * mm, "end": v(-60, 37.3) * mm});
            skArc(sketch, "E80.5", {"start": v(52.38, 47.01) * mm, "mid": v(0, 53.33) * mm, "end": v(-52.38, 47.01) * mm});
            skArc(sketch, "E80.6", {"start": v(60, 37.3) * mm, "mid": v(57.87, 43.47) * mm, "end": v(52.38, 47.01) * mm});
            skCircle(sketch, "E80.7", {"center": v(60, 53.33) * mm, "radius": 4 * mm});
            skArc(sketch, "E80.8", {"start": v(52.38, -47.01) * mm, "mid": v(57.87, -43.47) * mm, "end": v(60, -37.3) * mm});
            skCircle(sketch, "E80.9", {"center": v(60, -53.33) * mm, "radius": 4 * mm});
            skCircle(sketch, "E80.10", {"center": v(-60, -53.33) * mm, "radius": 4 * mm});
            skCircle(sketch, "E80.11", {"center": v(-60, 53.33) * mm, "radius": 4 * mm});
            skLineSegment(sketch, "E81", {"start": v(0, 80) * mm, "end": v(0, 110) * mm, "construction": true});
            skCircle(sketch, "E82", {"center": v(0, 110) * mm, "radius": 6 * mm});
            skLineSegment(sketch, "E83", {"start": v(-33, 80) * mm, "end": v(-15, 98) * mm});
            skLineSegment(sketch, "E84", {"start": v(33, 80) * mm, "end": v(15, 98) * mm});
            skLineSegment(sketch, "E85", {"start": v(-15, 98) * mm, "end": v(-15, 110) * mm});
            skLineSegment(sketch, "E86", {"start": v(15, 98) * mm, "end": v(15, 110) * mm});
            skArc(sketch, "E87", {"start": v(15, 110) * mm, "mid": v(0, 125) * mm, "end": v(-15, 110) * mm});
            skLineSegment(sketch, "E88", {"start": v(-90, 0) * mm, "end": v(90, 0) * mm, "construction": true});
            skLineSegment(sketch, "E89.MirrorCS", {"start": v(0, -80) * mm, "end": v(0, -110) * mm, "construction": true});
            skLineSegment(sketch, "E90.MirrorCS", {"start": v(-33, -80) * mm, "end": v(-15, -98) * mm});
            skLineSegment(sketch, "E91.MirrorCS", {"start": v(-15, -98) * mm, "end": v(-15, -110) * mm});
            skArc(sketch, "E92.MirrorCS", {"start": v(15, -110) * mm, "mid": v(0, -125) * mm, "end": v(-15, -110) * mm});
            skLineSegment(sketch, "E93.MirrorCS", {"start": v(33, -80) * mm, "end": v(15, -98) * mm});
            skCircle(sketch, "E94.MirrorC", {"center": v(0, -110) * mm, "radius": 6 * mm});
            skLineSegment(sketch, "E95.MirrorCS", {"start": v(15, -98) * mm, "end": v(15, -110) * mm});
            skSolve(sketch);
        }
        {
            var Q0;
            Q0 = qSketchRegion(id + "F16", true);
            var Q1;
            Q1=makeQuery(id+"F2.opExtrude","CAP_FACE",FACE,{"disambiguationData":[OSD([sQuery(id+"F0.wireOp",EDGE,"E12"),sQuery(id+"F0.wireOp",EDGE,"E13"),sQuery(id+"F0.wireOp",EDGE,"E14"),sQuery(id+"F0.wireOp",EDGE,"E15"),sQuery(id+"F0.wireOp",EDGE,"E17.filletArc"),sQuery(id+"F0.wireOp",EDGE,"E18.filletArc"),sQuery(id+"F0.wireOp",EDGE,"E19.filletArc"),sQuery(id+"F0.wireOp",EDGE,"E20.filletArc"),sQuery(id+"F0.wireOp",EDGE,"E25.0"),sQuery(id+"F0.wireOp",EDGE,"E25.1"),sQuery(id+"F0.wireOp",EDGE,"E25.2"),sQuery(id+"F0.wireOp",EDGE,"E25.3"),sQuery(id+"F0.wireOp",EDGE,"E25.4"),sQuery(id+"F0.wireOp",EDGE,"E25.5"),sQuery(id+"F0.wireOp",EDGE,"E25.6"),sQuery(id+"F0.wireOp",EDGE,"E25.7")])],"isStart":false});
            extrude(context, id + "F17", {"entities" : qUnion([Q0]), "endBound" : BoundingType.UP_TO_SURFACE, "endBoundEntityFace" : qUnion([Q1]), "depth" : 25 * mm});
        }
    });
